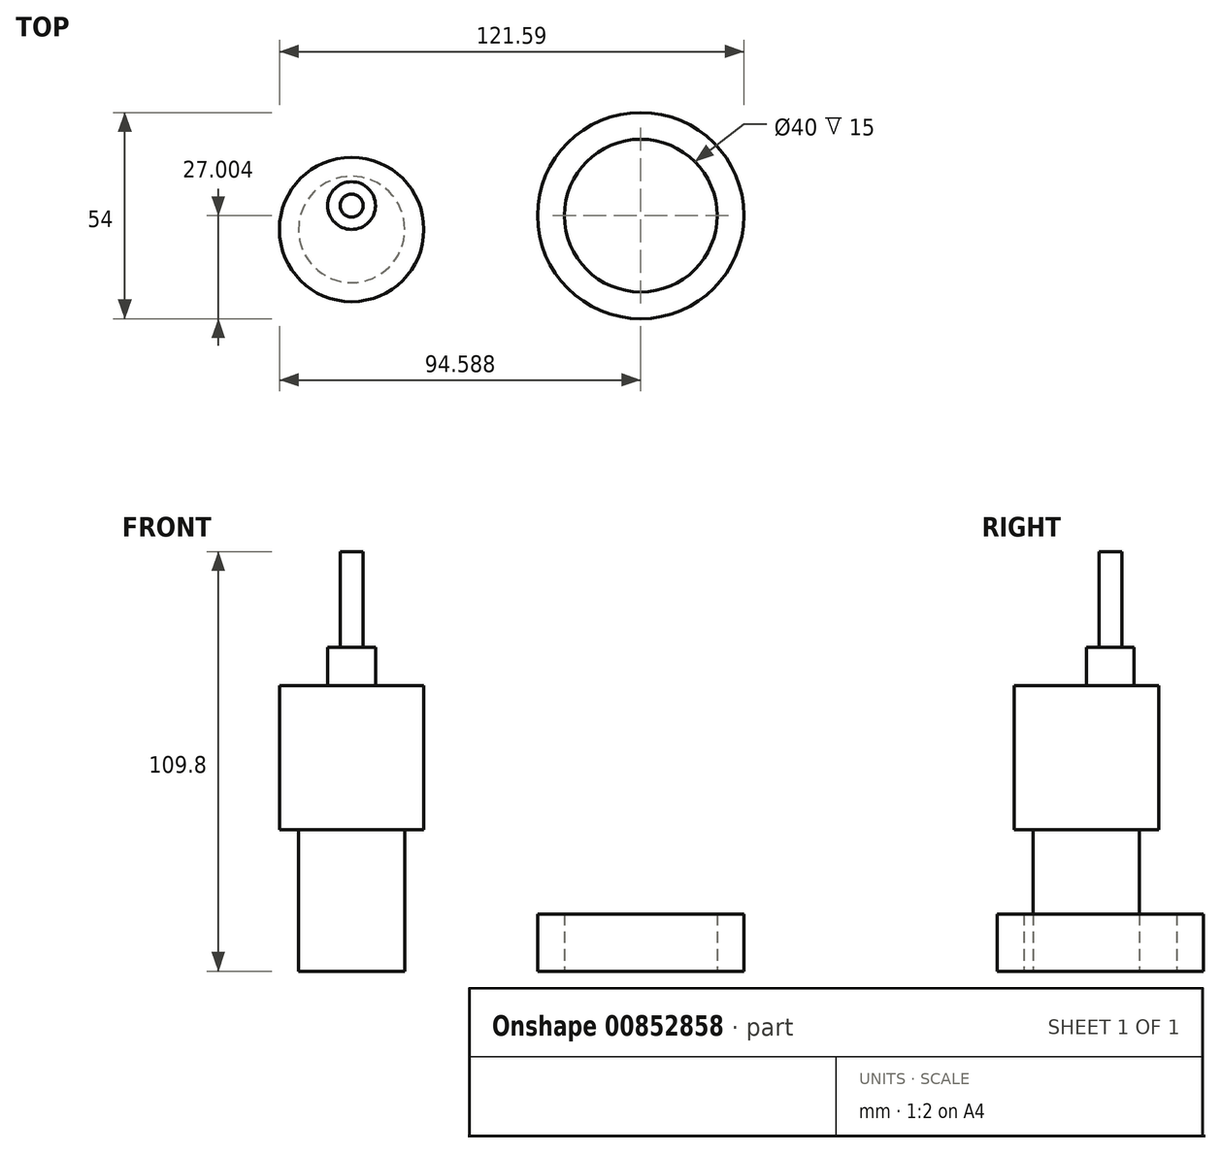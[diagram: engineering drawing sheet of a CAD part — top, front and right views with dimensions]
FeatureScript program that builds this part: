
annotation { "Feature Type Name" : "Feature", "Feature Type Description" : "" }
export const myFeature = defineFeature(function(context is Context, id is Id, definition is map)
    precondition{}
    {
        {
            var Q0;
            Q0=qCreatedBy(makeId("Top.planeOp"),FACE);
            var sketch = newSketch(context, id + "F0", { "sketchPlane" : qUnion([Q0])});
            skCircle(sketch, "E0", {"center": v(0, 0) * mm, "radius": 13.9 * mm});
            skSolve(sketch);
        }
        {
            var Q0;
            Q0 = qSketchRegion(id + "F0", true);
            extrude(context, id + "F1", {"entities" : qUnion([Q0]), "depth" : 37 * mm, "offsetDistance" : 25 * mm});
        }
        {
            var Q0;
            Q0=makeQuery(id+"F1.opExtrude","CAP_FACE",FACE,{"disambiguationData":[OSD([sQuery(id+"F0.wireOp",EDGE,"E0")])],"isStart":false});
            var sketch = newSketch(context, id + "F2", { "sketchPlane" : qUnion([Q0])});
            skCircle(sketch, "E1", {"center": v(0, 0) * mm, "radius": 18.9 * mm});
            skSolve(sketch);
        }
        {
            var Q0;
            Q0 = qSketchRegion(id + "F2", true);
            extrude(context, id + "F3", {"entities" : qUnion([Q0]), "operationType" : NewBodyOperationType.ADD, "depth" : 37.8 * mm, "offsetDistance" : 25 * mm});
        }
        {
            var Q0;
            Q0=makeQuery(id+"F3.opExtrude","CAP_FACE",FACE,{"disambiguationData":[OSD([sQuery(id+"F2.wireOp",EDGE,"E1")])],"isStart":false});
            var sketch = newSketch(context, id + "F4", { "sketchPlane" : qUnion([Q0])});
            skLineSegment(sketch, "E2", {"start": v(-18.9, 0) * mm, "end": v(18.9, 0) * mm, "construction": true});
            skPoint(sketch, "E3", {"position": v(0, -6.25) * mm});
            skLineSegment(sketch, "E4.0", {"start": v(-18.9, 6.25) * mm, "end": v(18.9, 6.25) * mm, "construction": true});
            skCircle(sketch, "E5", {"center": v(0, 6.25) * mm, "radius": 6.25 * mm});
            skSolve(sketch);
        }
        {
            var Q0;
            Q0 = qSketchRegion(id + "F4", true);
            extrude(context, id + "F5", {"entities" : qUnion([Q0]), "operationType" : NewBodyOperationType.ADD, "depth" : 10 * mm, "offsetDistance" : 25 * mm});
        }
        {
            var Q0;
            Q0=makeQuery(id+"F5.opExtrude","CAP_FACE",FACE,{"disambiguationData":[OSD([sQuery(id+"F4.wireOp",EDGE,"E5")])],"isStart":false});
            var sketch = newSketch(context, id + "F6", { "sketchPlane" : qUnion([Q0])});
            skCircle(sketch, "E6", {"center": v(0, 6.25) * mm, "radius": 3 * mm});
            skSolve(sketch);
        }
        {
            var Q0;
            Q0 = qSketchRegion(id + "F6", true);
            extrude(context, id + "F7", {"entities" : qUnion([Q0]), "depth" : 25 * mm, "offsetDistance" : 25 * mm});
        }
        {
            var Q0;
            Q0=qCreatedBy(makeId("Top.planeOp"),FACE);
            var sketch = newSketch(context, id + "F8", { "sketchPlane" : qUnion([Q0])});
            skCircle(sketch, "E7", {"center": v(75.69, 3.63) * mm, "radius": 27 * mm});
            skCircle(sketch, "E8", {"center": v(75.69, 3.63) * mm, "radius": 20 * mm});
            skSolve(sketch);
        }
        {
            var Q0;
            Q0=makeQuery(id+"F8.imprint","IMPRINT",FACE,{"disambiguationData":[TD([[makeQuery(id+"F8.imprint","IMPRINT",EDGE,{"derivedFrom":sQuery(id+"F8.wireOp",EDGE,"E7")}),1.0]])]});
            extrude(context, id + "F9", {"entities" : qUnion([Q0]), "depth" : 15 * mm, "offsetDistance" : 25 * mm});
        }
    });
